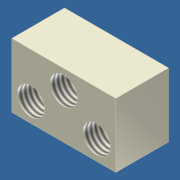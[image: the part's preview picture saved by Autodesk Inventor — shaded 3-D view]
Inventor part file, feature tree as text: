
AUTODESK INVENTOR PART (.ipt)
format: ipt  version: unknown  size: 200,704 bytes
history: native  units: in
note: dims shown in document units (in); Inventor stores cm internally (conversion verified against a paired STEP export)
features: thread x5, extrude x3, sketch x3
ambient origin geometry x8: Origin, YZ Plane, XZ Plane, XY Plane, X Axis, Y Axis, Z Axis, Center Point
bodies: Solid1 (feature_tree)
feature tree (11):
  extrude  "Extrusion1"  Depth=1.0in
  extrude  "Extrusion2"  Depth=0.425in
  thread  "Thread1"  [1 undecoded]
  thread  "Thread2"  [1 undecoded]
  thread  "Thread3"  [1 undecoded]
  extrude  "Extrusion3"  Depth=0.3in
  thread  "Thread4"  [1 undecoded]
  thread  "Thread5"  [1 undecoded]
  sketch  "Sketch1"  dims[d0=1.625in d1=1.0in]
  sketch  "Sketch2"  dims[d2=0.825in d3=0.0in d4=0.425in d5=0.3in d6=0.3in d7=0.3in]
  sketch  "Sketch3"  dims[d8=0.3in d9=0.3in d10=0.375in d11=0.0in d12=1.0in d13=0.0in d14=1.0in d15=0.0in d16=1.0in d17=0.0in d18=0.425in d19=0.75in d20=0.4375in d21=0.375in d22=0.0in d23=1.0in d24=0.0in d25=1.0in d26=0.0in]
note: 5 required parameter values undecoded (feature->parameter linkage not recoverable at this tier; creation-order binding heuristic only, values carry confidence <= 0.55)
